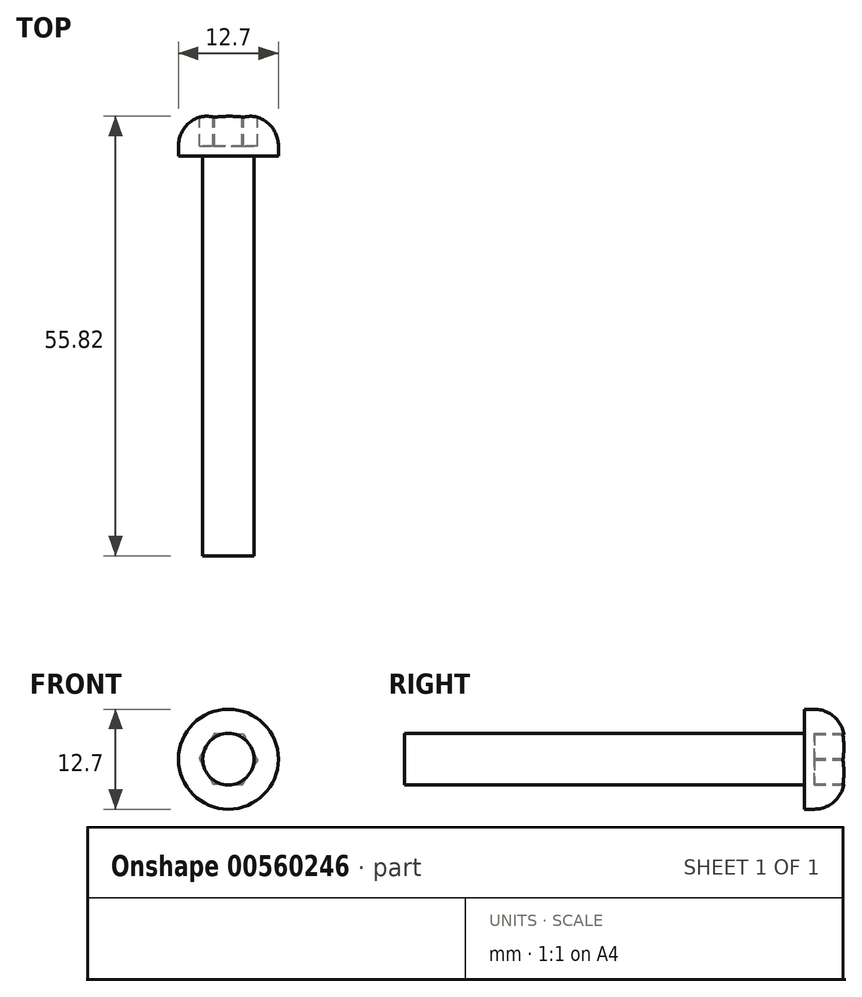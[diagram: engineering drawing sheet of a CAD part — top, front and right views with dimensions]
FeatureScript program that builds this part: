
annotation { "Feature Type Name" : "Feature", "Feature Type Description" : "" }
export const myFeature = defineFeature(function(context is Context, id is Id, definition is map)
    precondition{}
    {
        {
            var Q0;
            Q0=qCreatedBy(makeId("Front.planeOp"),FACE);
            var sketch = newSketch(context, id + "F0", { "sketchPlane" : qUnion([Q0])});
            skCircle(sketch, "E0", {"center": v(0, 0) * mm, "radius": 3.26 * mm});
            skSolve(sketch);
        }
        {
            var Q0;
            Q0=makeQuery(id+"F0.imprint","IMPRINT",FACE,{"disambiguationData":[TD([[makeQuery(id+"F0.imprint","IMPRINT",EDGE,{"derivedFrom":sQuery(id+"F0.wireOp",EDGE,"E0")}),1.0]])]});
            extrude(context, id + "F1", {"entities" : qUnion([Q0]), "depth" : 50.8 * mm, "offsetDistance" : 25.4 * mm});
        }
        {
            var Q0;
            Q0=makeQuery(id+"F1.opExtrude","CAP_FACE",FACE,{"disambiguationData":[OSD([sQuery(id+"F0.wireOp",EDGE,"E0")])],"isStart":true});
            var sketch = newSketch(context, id + "F2", { "sketchPlane" : qUnion([Q0])});
            skCircle(sketch, "E1", {"center": v(0, 0) * mm, "radius": 6.35 * mm});
            skSolve(sketch);
        }
        {
            var Q0;
            Q0=makeQuery(id+"F2.imprint","IMPRINT",FACE,{"disambiguationData":[TD([[makeQuery(id+"F2.imprint","IMPRINT",EDGE,{"derivedFrom":sQuery(id+"F2.wireOp",EDGE,"E1")}),1.0]])]});
            var Q1;
            Q1=makeQuery(id+"F2.imprint","IMPRINT",FACE,{"disambiguationData":[TD([[makeQuery(id+"F2.imprint","IMPRINT",EDGE,{"derivedFrom":makeQuery(id+"F1.opExtrude","CAP_EDGE",EDGE,{"disambiguationData":[OSD([sQuery(id+"F0.wireOp",EDGE,"E0")])],"isStart":true})}),-1.0]])]});
            extrude(context, id + "F3", {"entities" : qUnion([Q0, Q1]), "operationType" : NewBodyOperationType.ADD, "depth" : 5.08 * mm, "offsetDistance" : 25.4 * mm});
        }
        {
            var Q0;
            Q0=makeQuery(id+"F3.opExtrude","CAP_FACE",FACE,{"disambiguationData":[OSD([sQuery(id+"F2.wireOp",EDGE,"E1")])],"isStart":false});
            var sketch = newSketch(context, id + "F4", { "sketchPlane" : qUnion([Q0])});
            skCircle(sketch, "E2.cCircle", {"center": v(0, 0) * mm, "radius": 3.2 * mm, "construction": true});
            skLineSegment(sketch, "E2.0", {"start": v(-3.7, -0.1) * mm, "end": v(-1.94, 3.15) * mm});
            skLineSegment(sketch, "E2.1", {"start": v(-1.94, 3.15) * mm, "end": v(1.76, 3.25) * mm});
            skLineSegment(sketch, "E2.2", {"start": v(1.76, 3.25) * mm, "end": v(3.7, 0.1) * mm});
            skLineSegment(sketch, "E2.3", {"start": v(3.7, 0.1) * mm, "end": v(1.94, -3.15) * mm});
            skLineSegment(sketch, "E2.4", {"start": v(1.94, -3.15) * mm, "end": v(-1.76, -3.25) * mm});
            skLineSegment(sketch, "E2.5", {"start": v(-1.76, -3.25) * mm, "end": v(-3.7, -0.1) * mm});
            skPoint(sketch, "E2.0.midPoint", {"position": v(-2.81, 1.52) * mm});
            skSolve(sketch);
        }
        {
            var Q0;
            Q0=makeQuery(id+"F4.imprint","IMPRINT",FACE,{"disambiguationData":[TD([[makeQuery(id+"F4.imprint","IMPRINT",EDGE,{"derivedFrom":sQuery(id+"F4.wireOp",EDGE,"E2.0")}),-1.0]])]});
            extrude(context, id + "F5", {"entities" : qUnion([Q0]), "operationType" : NewBodyOperationType.REMOVE, "oppositeDirection" : true, "depth" : 3.8 * mm, "offsetDistance" : 25.4 * mm});
        }
        {
            var Q0;
            Q0=makeQuery(id+"F3.opExtrude","CAP_EDGE",EDGE,{"disambiguationData":[OSD([sQuery(id+"F2.wireOp",EDGE,"E1")])],"isStart":false});
            fillet(context, id + "F6", {"entities" : qUnion([Q0]), "radius" : 3.8 * mm, "tangentPropagation" : true, "allowEdgeOverflow" : false});
        }
    });
